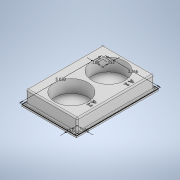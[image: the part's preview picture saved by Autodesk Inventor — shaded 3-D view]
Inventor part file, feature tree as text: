
AUTODESK INVENTOR PART (.ipt)
format: ipt  version: 2020 (Build 240168000, 168)  size: 422,912 bytes
history: native  units: in
note: dims shown in document units (in); Inventor stores cm internally (conversion verified against a paired STEP export)
features: extrude x5, sketch x4, fillet x3
ambient origin geometry x8: Origin, YZ Plane, XZ Plane, XY Plane, X Axis, Y Axis, Z Axis, Center Point
bodies: Solid1 (feature_tree)
feature tree (12):
  sketch  "Sketch1"  dims[d0=3.3661in d1=5.0295in]
  extrude  "Extrusion1"  Depth=5.0295in
  extrude  "Extrusion2"  Depth=0.1526in
  extrude  "Extrusion3"  Depth=0.1526in
  extrude  "Extrusion4"  Depth=0.1181in TaperAngle=0.0deg
  fillet  "Fillet1"  Radius=1.5748in
  fillet  "Fillet2"  Radius=1.2205in
  fillet  "Fillet3"  Radius=2.0506in
  extrude  "Extrusion5"  Depth=0.3937in
  sketch  "Sketch2"  dims[d2=0.1083in d3=0.1526in]
  sketch  "Sketch3"  dims[d4=0.1083in d5=0.1526in]
  sketch  "Sketch4"  dims[d6=0.7874in d7=0.0in d8=0.1181in d9=0.0in d10=1.5748in d11=1.2205in d12=2.0506in d13=0.3937in d15=1.5748in d16=0.7874in d18=2.2835in d21=0.7874in d22=0.0in d32=0.1181in d33=0.1181in d34=0.1181in d35=0.1181in d36=0.7087in d37=0.0in d38=0.125in d39=0.125in d40=0.0787in d41=0.0394in d42=0.0in d43=2.2872in d44=2.2872in]
